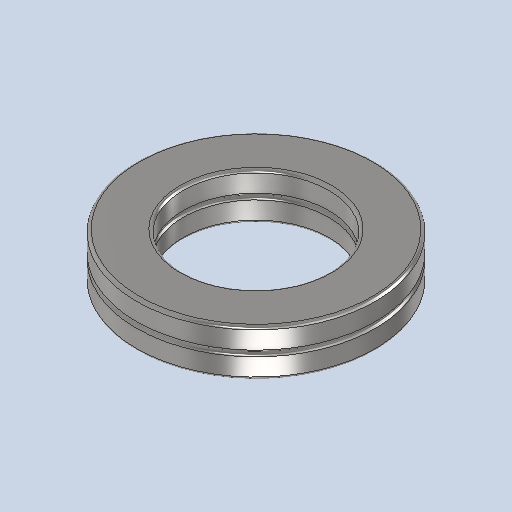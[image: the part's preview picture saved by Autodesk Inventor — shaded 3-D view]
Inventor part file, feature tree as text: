
AUTODESK INVENTOR PART (.ipt)
format: ipt  version: 2024.2 (Build 282272000, 272)  size: 175,616 bytes
history: native  units: mm
features: revolve x1, sketch x1
ambient origin geometry x8: Origin, YZ Plane, XZ Plane, XY Plane, X Axis, Y Axis, Z Axis, Center Point
bodies: Solid1 (feature_tree)
feature tree (2):
  revolve  "Revolution1"  [1 undecoded]
  sketch  "Sketch1"  dims[d0=0.5mm d1=25.0mm d2=41.0mm d4=8.0mm d5=90.0deg]
note: 1 required parameter value undecoded (feature->parameter linkage not recoverable at this tier; creation-order binding heuristic only, values carry confidence <= 0.55)
